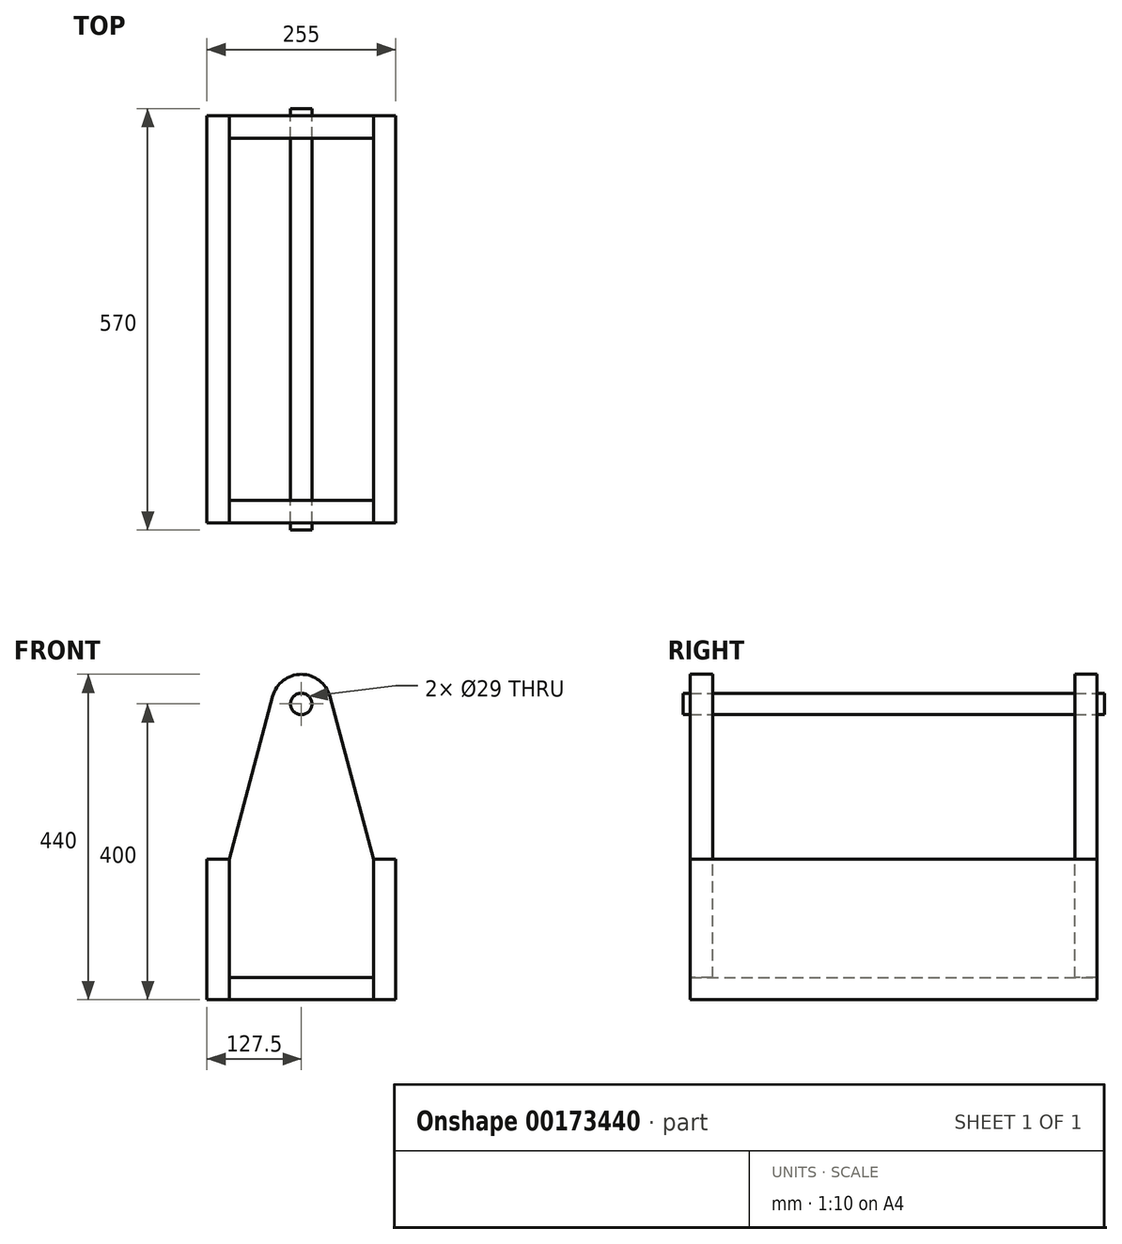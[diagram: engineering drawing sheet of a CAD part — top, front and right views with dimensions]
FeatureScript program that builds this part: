
annotation { "Feature Type Name" : "Feature", "Feature Type Description" : "" }
export const myFeature = defineFeature(function(context is Context, id is Id, definition is map)
    precondition{}
    {
        {
            var Q0;
            Q0=qCreatedBy(makeId("Front.planeOp"),FACE);
            var sketch = newSketch(context, id + "F0", { "sketchPlane" : qUnion([Q0])});
            skLineSegment(sketch, "E0.bottom", {"start": v(-97.5, 0) * mm, "end": v(97.5, 0) * mm});
            skLineSegment(sketch, "E0.top", {"start": v(-97.5, 30) * mm, "end": v(97.5, 30) * mm});
            skLineSegment(sketch, "E0.left", {"start": v(-97.5, 0) * mm, "end": v(-97.5, 30) * mm});
            skLineSegment(sketch, "E0.right", {"start": v(97.5, 0) * mm, "end": v(97.5, 30) * mm});
            skSolve(sketch);
        }
        {
            var Q0;
            Q0 = qSketchRegion(id + "F0", true);
            extrude(context, id + "F1", {"entities" : qUnion([Q0]), "endBound" : BoundingType.SYMMETRIC, "depth" : 550 * mm});
        }
        {
            var Q0;
            Q0=makeQuery(id+"F1.opExtrude","CAP_FACE",FACE,{"disambiguationData":[OSD([sQuery(id+"F0.wireOp",EDGE,"E0.bottom"),sQuery(id+"F0.wireOp",EDGE,"E0.top"),sQuery(id+"F0.wireOp",EDGE,"E0.left"),sQuery(id+"F0.wireOp",EDGE,"E0.right")])],"isStart":false});
            var sketch = newSketch(context, id + "F2", { "sketchPlane" : qUnion([Q0])});
            skLineSegment(sketch, "E1.bottom", {"start": v(-125.35, -30) * mm, "end": v(124.65, -30) * mm});
            skLineSegment(sketch, "E1.top", {"start": v(-125.35, 160) * mm, "end": v(124.65, 160) * mm});
            skLineSegment(sketch, "E1.left", {"start": v(-125.35, -30) * mm, "end": v(-125.35, 160) * mm});
            skLineSegment(sketch, "E1.right", {"start": v(124.65, -30) * mm, "end": v(124.65, 160) * mm});
            skSolve(sketch);
        }
        {
            var Q0;
            Q0=qCreatedBy(makeId("Front.planeOp"),FACE);
            var sketch = newSketch(context, id + "F3", { "sketchPlane" : qUnion([Q0])});
            skLineSegment(sketch, "E2.bottom", {"start": v(-97.5, 0) * mm, "end": v(-127.5, 0) * mm});
            skLineSegment(sketch, "E2.top", {"start": v(-97.5, 190) * mm, "end": v(-127.5, 190) * mm});
            skLineSegment(sketch, "E2.left", {"start": v(-97.5, 0) * mm, "end": v(-97.5, 190) * mm});
            skLineSegment(sketch, "E2.right", {"start": v(-127.5, 0) * mm, "end": v(-127.5, 190) * mm});
            skSolve(sketch);
        }
        {
            var Q0;
            Q0 = qSketchRegion(id + "F3", true);
            extrude(context, id + "F4", {"entities" : qUnion([Q0]), "endBound" : BoundingType.SYMMETRIC, "depth" : 550 * mm});
        }
        {
            var Q0;
            Q0=makeQuery(id+"F4.opExtrude","SWEPT_BODY",BODY,{"disambiguationData":[OSD([sQuery(id+"F3.wireOp",EDGE,"E2.bottom"),sQuery(id+"F3.wireOp",EDGE,"E2.top"),sQuery(id+"F3.wireOp",EDGE,"E2.left"),sQuery(id+"F3.wireOp",EDGE,"E2.right")])]});
            transform(context, id + "F5", {"entities" : qUnion([Q0]), "transformType" : TransformType.TRANSLATION_3D, "dx" : 225 * mm, "dy" : 0 * mm, "dz" : 0 * mm, "makeCopy" : true});
        }
        {
            var Q0;
            Q0=makeQuery(id+"F2.imprint","IMPRINT",FACE,{"disambiguationData":[TD([[makeQuery(id+"F2.imprint","IMPRINT",EDGE,{"derivedFrom":makeQuery(id+"F1.opExtrude","CAP_EDGE",EDGE,{"disambiguationData":[OSD([sQuery(id+"F0.wireOp",EDGE,"E0.bottom")])],"isStart":false})}),1.0]])]});
            var sketch = newSketch(context, id + "F6", { "sketchPlane" : qUnion([Q0])});
            skLineSegment(sketch, "E3", {"start": v(97.5, 30) * mm, "end": v(97.5, 190) * mm});
            skLineSegment(sketch, "E4", {"start": v(97.5, 190) * mm, "end": v(38.64, 410.32) * mm});
            skLineSegment(sketch, "E5", {"start": v(-97.5, 30) * mm, "end": v(-97.5, 190) * mm});
            skLineSegment(sketch, "E6", {"start": v(-97.5, 190) * mm, "end": v(-38.64, 410.32) * mm});
            skArc(sketch, "E7", {"start": v(38.64, 410.32) * mm, "mid": v(0, 440) * mm, "end": v(-38.64, 410.32) * mm});
            skLineSegment(sketch, "E8", {"start": v(-97.5, 30) * mm, "end": v(97.5, 30) * mm});
            skCircle(sketch, "E9", {"center": v(0, 400) * mm, "radius": 14.5 * mm});
            skSolve(sketch);
        }
        {
            var Q0;
            Q0 = qSketchRegion(id + "F6", true);
            extrude(context, id + "F7", {"entities" : qUnion([Q0]), "oppositeDirection" : true, "depth" : 30 * mm});
        }
        {
            var Q0;
            Q0=makeQuery(id+"F7.opExtrude","SWEPT_BODY",BODY,{"disambiguationData":[OSD([sQuery(id+"F6.wireOp",EDGE,"E3"),sQuery(id+"F6.wireOp",EDGE,"E4"),sQuery(id+"F6.wireOp",EDGE,"E5"),sQuery(id+"F6.wireOp",EDGE,"E6"),sQuery(id+"F6.wireOp",EDGE,"E7"),sQuery(id+"F6.wireOp",EDGE,"E8"),sQuery(id+"F6.wireOp",EDGE,"E9")])]});
            transform(context, id + "F8", {"entities" : qUnion([Q0]), "transformType" : TransformType.TRANSLATION_3D, "dx" : 0 * mm, "dy" : 520 * mm, "dz" : 0 * mm, "makeCopy" : true});
        }
        {
            var Q0;
            Q0=qCreatedBy(makeId("Front.planeOp"),FACE);
            var sketch = newSketch(context, id + "F9", { "sketchPlane" : qUnion([Q0])});
            skCircle(sketch, "E10.0", {"center": v(0, 400) * mm, "radius": 14.5 * mm});
            skSolve(sketch);
        }
        {
            var Q0;
            Q0 = qSketchRegion(id + "F9", true);
            extrude(context, id + "F10", {"entities" : qUnion([Q0]), "endBound" : BoundingType.SYMMETRIC, "depth" : 570 * mm});
        }
    });
